# Revit family: Midmark - Tapered Electric Lift Table
name_source: partatom
category: Specialty Equipment
revit_build: Autodesk Revit 2017 (Build: 20190507_1515(x64)
units: mm (PartAtom-declared; Revit-internal decimal feet)

## family parameters
Always vertical = Yes
Cut with Voids When Loaded = No
OmniClass Number = 23.25.61.00
Part Type = Normal
Room Calculation Point = No
Round Connector Dimension = Use Diameter
Shared = No
Work Plane-Based = No

## types (4) — shared parameters
Back Board Material = Stainless Steel, Polished
Depth = 2' - 7"
Exam Table Material = Stainless Steel, Polished
Height = 7' - 0 1/2"
Lift Column Material = Stainless Steel, Polished
Manufacturer = MIDMARK
Max. Table Top Height w/out Scale = 3' - 4"
Min. Table Top Height w/out Scale = 0' - 8 1/2"
Pedestal Base Material = Steel, Paint Finish, Black, Matte
Pedestal Width = 3' - 0"
Table Depth = 3' - 8"
Table Top Frame Material = Steel, Paint Finish, Black, Matte
Table work Ht = 3' - 0"
Tie-Down Rail Material = Stainless Steel, Polished
Width = 1' - 10"

## per-type parameters (varying)
| type | Foot Control | Model | Scale | Type Comments |
| Stainless Steel Top w/ Hand Control | No | 101-5640-01 | No | Tapered Electric Lift Exam Table, 44"L x 22"W Stainless Steel Top with Hand Control |
| Stainless Steel Top w/ Foot Control | Yes | 101-5640-07 | No | Tapered Electric Lift Table, 44"L x 22"W Stainless Steel Top with Foot Control |
| Stainless Steel Top w/ Hand Control & Scale | No | 110-3210-00 | Yes | Tapered Electric Lift Exam Table, 44"L x 22"W Stainless Steel Top with Hand Control and Built-in Scale |
| Stainless Steel Top w/ Foot Control & Scale | Yes | 110-3210-01 | Yes | Tapered Electric Lift Table, 44"L x 22"W Stainless Steel Top with Foot Control and Built-in Scale |

## geometry (parser evidence)
native form markers: Sweep x2
no freeform markers — native parametric forms only
